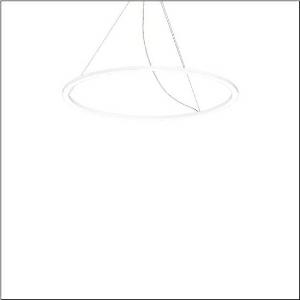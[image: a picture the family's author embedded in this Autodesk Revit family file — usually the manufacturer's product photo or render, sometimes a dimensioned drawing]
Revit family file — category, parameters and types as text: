
# Revit family: silica_r__21_ring-d_5pjbd3d1004a_5ef5
name_source: partatom
category: Lighting Fixtures
units: mm (PartAtom-declared; Revit-internal decimal feet)

## family parameters
Cut with Voids When Loaded = No
Host = Face
Light Source = No
Part Type = Normal
Room Calculation Point = No
Round Connector Dimension = Use Diameter
Shared = No

## types (1)
- Silica® 21 Ring-D (1 x LED, 8050 lm, 94 W, 3000K)
    Apparent Load = 94 VA
    CIE Flux Codes = 37 69 92 100 100
    Color Rendering = 80
    Color Temperature = 3000K
    Default Elevation = 1800 mm
    Description = Silica® 21 Ring-D, suspended luminaire, of PMMA, frosted, light emission: ring underside luminous distribution, primary light characteristic: symmetric, installation type: suspended mounting, LED, rated luminous flux: 8.050lm, luminous efficacy: 86lm/W, light colour: 830, colour temperature: 3000K, control gear: DALI 2, with terminal, 5-pole, mains connection: 230V, AC/DC, 0/50..60Hz, rated input power: 94W, housing, of extruded aluminium section, traffic white (RAL 9016), diameter: 1.100mm, ceiling canopy, traffic white (RAL 9016), protection rating (lamp compartment): IP40, insulation class (complete): insulation class I (protective earthing), certification: CE, impact resistance: IK02, permissible operating ambient temperature: 0..+35°C, packaging unit: 1 piece
    Height = 25 mm  [stored 0.082021 ft]
    Lamp = 1 x LED
    Lamp Light Flux = 8050 lm
    Lamp Power = 94 W
    Lamp count = 1
    Length = 1100 mm
    Luminous efficacy = 86 lm/W
    Manufacturer = Siteco
    ModVariant = No
    Model = 5PJBD3D1004A
    Mounting Place = Ceiling
    Mounting Type = Pendant
    Number of Poles = 1
    OnlyDefault = Yes
    Power Factor = 1
    Product Name = Silica® 21 Ring-D
    Product group = suspended luminaire
    ProductGroupID = 905
    Protection Class = Protection class I
    Protection Degree = IP 40
    RLX_Detail_Level = 1
    RLX_Emergency_Light_Flux = 0 lm
    RLX_Emergency_Type = 0
    RLX_Emergency_Type_DB = No
    RlxData = <blob elided: 12517 chars, md5=73bfdc2a>
    Socket = socket
    Standby Power = 0 W
    System Light Flux = 8050 lm
    System Power = 94 W
    Type Comments = Product without accessories
    Type Image = l_1258355.jpg
    URL = http://relux.com
    VarID = ---
    Voltage = 0 V
    Weight = 0.00 kg
    Width = 0 mm  [stored 0 ft]

note: [stored X ft] marks values corroborated as IEEE doubles in the binary element streams (Revit-internal decimal feet)

## geometry (parser evidence)
native form markers: Sweep x9
no freeform markers — native parametric forms only
